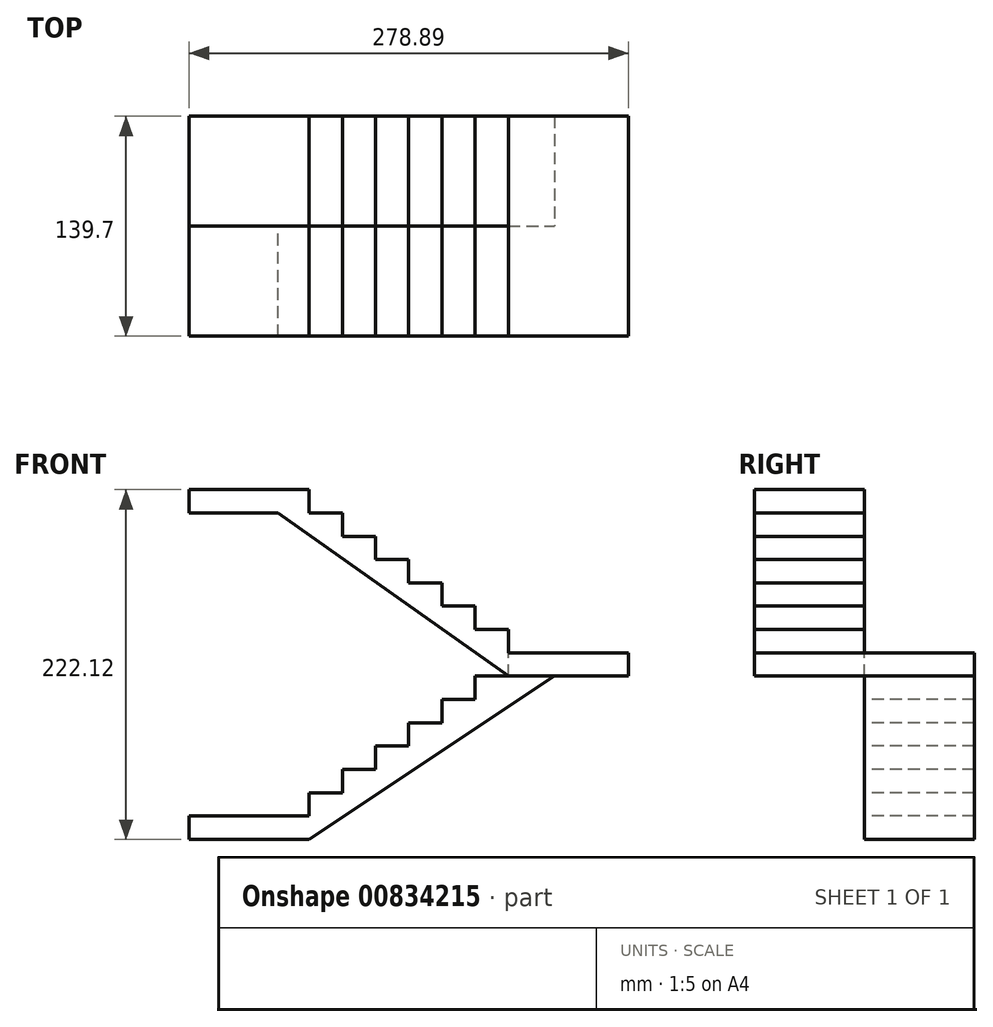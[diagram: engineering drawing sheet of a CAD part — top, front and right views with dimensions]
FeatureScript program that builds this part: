
annotation { "Feature Type Name" : "Feature", "Feature Type Description" : "" }
export const myFeature = defineFeature(function(context is Context, id is Id, definition is map)
    precondition{}
    {
        {
            var Q0;
            Q0=qCreatedBy(makeId("Front.planeOp"),FACE);
            var sketch = newSketch(context, id + "F0", { "sketchPlane" : qUnion([Q0])});
            skLineSegment(sketch, "E0", {"start": v(0, 0) * mm, "end": v(0, 14.8) * mm});
            skLineSegment(sketch, "E1", {"start": v(0, 14.8) * mm, "end": v(76.2, 14.8) * mm});
            skLineSegment(sketch, "E2", {"start": v(76.2, 14.8) * mm, "end": v(76.2, 29.62) * mm});
            skLineSegment(sketch, "E3", {"start": v(76.2, 29.62) * mm, "end": v(97.28, 29.62) * mm});
            skLineSegment(sketch, "E4", {"start": v(97.28, 29.62) * mm, "end": v(97.28, 44.42) * mm});
            skLineSegment(sketch, "E5", {"start": v(97.28, 44.42) * mm, "end": v(118.36, 44.42) * mm});
            skLineSegment(sketch, "E6", {"start": v(118.36, 44.42) * mm, "end": v(118.36, 59.23) * mm});
            skLineSegment(sketch, "E7", {"start": v(118.36, 59.23) * mm, "end": v(139.45, 59.23) * mm});
            skLineSegment(sketch, "E8", {"start": v(139.45, 59.23) * mm, "end": v(139.45, 74.04) * mm});
            skLineSegment(sketch, "E9", {"start": v(139.45, 74.04) * mm, "end": v(160.53, 74.04) * mm});
            skLineSegment(sketch, "E10", {"start": v(160.53, 74.04) * mm, "end": v(160.53, 88.85) * mm});
            skLineSegment(sketch, "E11", {"start": v(160.53, 88.85) * mm, "end": v(181.6, 88.85) * mm});
            skLineSegment(sketch, "E12", {"start": v(181.6, 88.85) * mm, "end": v(181.6, 103.66) * mm});
            skLineSegment(sketch, "E13", {"start": v(181.6, 103.66) * mm, "end": v(202.7, 103.66) * mm});
            skLineSegment(sketch, "E14", {"start": v(202.7, 103.66) * mm, "end": v(202.7, 118.47) * mm});
            skLineSegment(sketch, "E15", {"start": v(202.7, 118.47) * mm, "end": v(278.9, 118.47) * mm});
            skLineSegment(sketch, "E16", {"start": v(202.7, 118.47) * mm, "end": v(202.7, 133.27) * mm});
            skLineSegment(sketch, "E17", {"start": v(202.7, 133.27) * mm, "end": v(181.6, 133.27) * mm});
            skLineSegment(sketch, "E18", {"start": v(181.6, 133.27) * mm, "end": v(181.6, 148.08) * mm});
            skLineSegment(sketch, "E19", {"start": v(181.6, 148.08) * mm, "end": v(160.53, 148.08) * mm});
            skLineSegment(sketch, "E20", {"start": v(160.53, 148.08) * mm, "end": v(160.53, 162.9) * mm});
            skLineSegment(sketch, "E21", {"start": v(160.53, 162.9) * mm, "end": v(139.45, 162.9) * mm});
            skLineSegment(sketch, "E22", {"start": v(139.45, 162.9) * mm, "end": v(139.45, 177.7) * mm});
            skLineSegment(sketch, "E23", {"start": v(139.45, 177.7) * mm, "end": v(118.36, 177.7) * mm});
            skLineSegment(sketch, "E24", {"start": v(118.36, 177.7) * mm, "end": v(118.36, 192.5) * mm});
            skLineSegment(sketch, "E25", {"start": v(118.36, 192.5) * mm, "end": v(97.28, 192.5) * mm});
            skLineSegment(sketch, "E26", {"start": v(97.28, 192.5) * mm, "end": v(97.28, 207.31) * mm});
            skLineSegment(sketch, "E27", {"start": v(97.28, 207.31) * mm, "end": v(76.2, 207.31) * mm});
            skLineSegment(sketch, "E28", {"start": v(76.2, 207.31) * mm, "end": v(76.2, 222.12) * mm});
            skLineSegment(sketch, "E29", {"start": v(76.2, 222.12) * mm, "end": v(0, 222.12) * mm});
            skLineSegment(sketch, "E30", {"start": v(278.9, 118.47) * mm, "end": v(278.9, 103.66) * mm});
            skLineSegment(sketch, "E31", {"start": v(278.9, 103.66) * mm, "end": v(232.1, 103.66) * mm});
            skLineSegment(sketch, "E32", {"start": v(0, 0) * mm, "end": v(76.2, 0) * mm});
            skLineSegment(sketch, "E33", {"start": v(76.2, 0) * mm, "end": v(232.1, 103.66) * mm});
            skLineSegment(sketch, "E34", {"start": v(0, 222.12) * mm, "end": v(0, 207.31) * mm});
            skLineSegment(sketch, "E35", {"start": v(0, 207.31) * mm, "end": v(56.33, 207.31) * mm});
            skLineSegment(sketch, "E36", {"start": v(202.7, 103.66) * mm, "end": v(56.33, 207.31) * mm});
            skLineSegment(sketch, "E37", {"start": v(202.7, 103.66) * mm, "end": v(232.1, 103.66) * mm});
            skSolve(sketch);
        }
        {
            var Q0;
            Q0=makeQuery(id+"F0.imprint","IMPRINT",FACE,{"disambiguationData":[TD([[makeQuery(id+"F0.imprint","IMPRINT",EDGE,{"derivedFrom":sQuery(id+"F0.wireOp",EDGE,"E14")}),-1.0]])]});
            var Q1;
            Q1=makeQuery(id+"F0.imprint","IMPRINT",FACE,{"disambiguationData":[TD([[makeQuery(id+"F0.imprint","IMPRINT",EDGE,{"derivedFrom":sQuery(id+"F0.wireOp",EDGE,"E0")}),-1.0]])]});
            extrude(context, id + "F1", {"entities" : qUnion([Q0, Q1]), "oppositeDirection" : true, "depth" : 69.85 * mm, "offsetDistance" : 25.4 * mm});
        }
        {
            var Q0;
            Q0=makeQuery(id+"F0.imprint","IMPRINT",FACE,{"disambiguationData":[TD([[makeQuery(id+"F0.imprint","IMPRINT",EDGE,{"derivedFrom":sQuery(id+"F0.wireOp",EDGE,"E14")}),1.0]])]});
            var Q1;
            Q1=makeQuery(id+"F0.imprint","IMPRINT",FACE,{"disambiguationData":[TD([[makeQuery(id+"F0.imprint","IMPRINT",EDGE,{"derivedFrom":sQuery(id+"F0.wireOp",EDGE,"E14")}),-1.0]])]});
            extrude(context, id + "F2", {"entities" : qUnion([Q0, Q1]), "operationType" : NewBodyOperationType.ADD, "depth" : 69.85 * mm, "offsetDistance" : 25.4 * mm});
        }
    });
